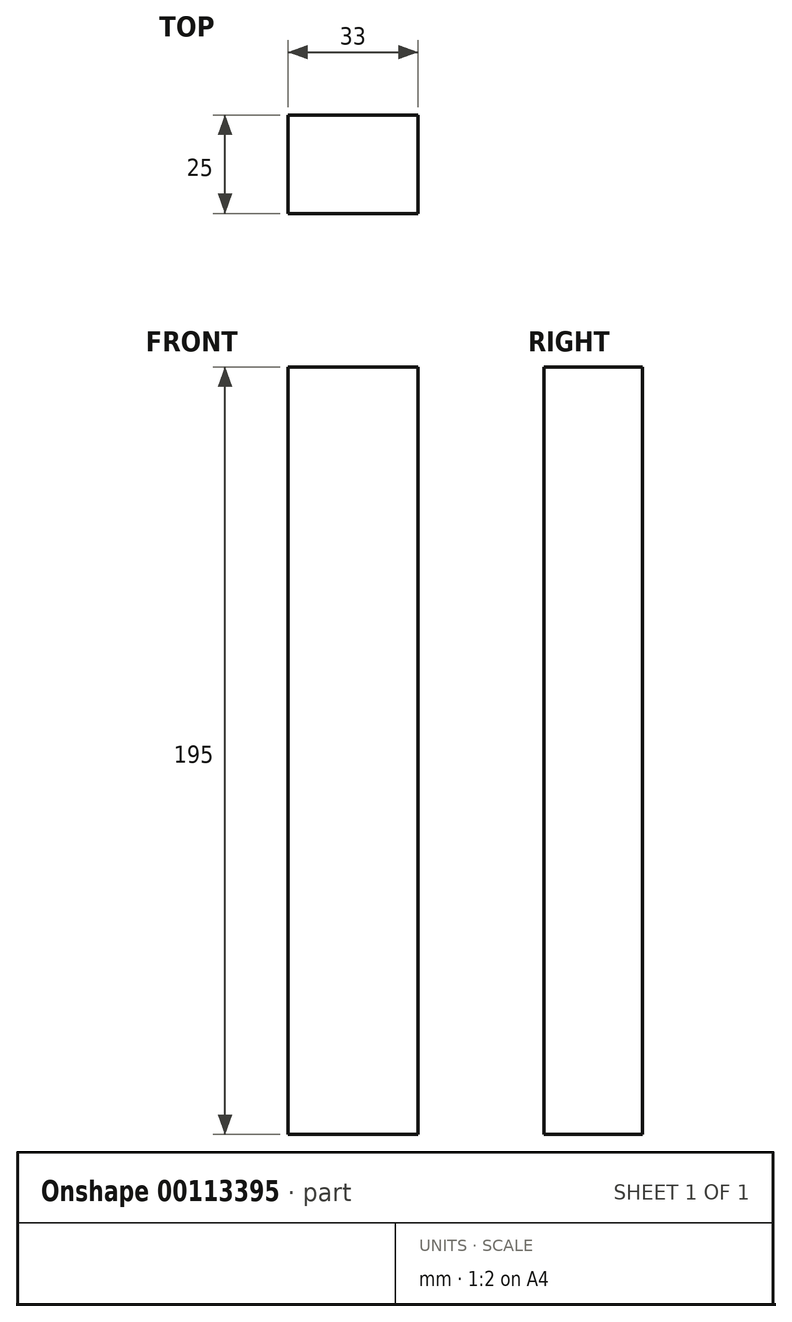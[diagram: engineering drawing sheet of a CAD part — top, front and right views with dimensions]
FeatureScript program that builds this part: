
annotation { "Feature Type Name" : "Feature", "Feature Type Description" : "" }
export const myFeature = defineFeature(function(context is Context, id is Id, definition is map)
    precondition{}
    {
        {
            var Q0;
            Q0=qCreatedBy(makeId("Front.planeOp"),FACE);
            var sketch = newSketch(context, id + "F0", { "sketchPlane" : qUnion([Q0])});
            skLineSegment(sketch, "E0", {"start": v(0, 0) * mm, "end": v(0, 195) * mm});
            skLineSegment(sketch, "E1", {"start": v(0, 195) * mm, "end": v(33, 195) * mm});
            skLineSegment(sketch, "E2", {"start": v(33, 195) * mm, "end": v(33, 0) * mm});
            skLineSegment(sketch, "E3", {"start": v(33, 0) * mm, "end": v(0, 0) * mm});
            skSolve(sketch);
        }
        {
            var Q0;
            Q0=makeQuery(id+"F0.imprint","IMPRINT",FACE,{"disambiguationData":[TD([[makeQuery(id+"F0.imprint","IMPRINT",EDGE,{"derivedFrom":sQuery(id+"F0.wireOp",EDGE,"E0")}),-1.0]])]});
            extrude(context, id + "F1", {"entities" : qUnion([Q0]), "depth" : 25 * mm});
        }
    });
